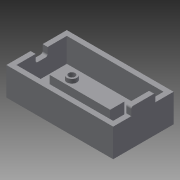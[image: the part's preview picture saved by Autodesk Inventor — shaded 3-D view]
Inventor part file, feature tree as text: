
AUTODESK INVENTOR PART (.ipt)
format: ipt  version: 2015 (Build 190159000, 159)  size: 167,424 bytes
history: native  units: mm
features: extrude x7, sketch x7, hole x1, fillet x1
ambient origin geometry x8: Origin, YZ Plane, XZ Plane, XY Plane, X Axis, Y Axis, Z Axis, Center Point
bodies: Volumenkörper1 (feature_tree)
feature tree (16):
  extrude  "Extrusion1"  Depth=53.0mm
  extrude  "Extrusion2"  Depth=25.0mm
  extrude  "Extrusion3"  Depth=2.5mm
  hole  "Bohrung1"  [1 undecoded]
  extrude  "Extrusion4"  Depth=12.0mm TaperAngle=0.0deg
  extrude  "Extrusion5"  Depth=30.0mm
  extrude  "Extrusion6"  Depth=9.0mm
  extrude  "Extrusion7"  Depth=9.0mm
  fillet  "Rundung1"  Radius=7.0mm
  sketch  "Skizze1"  dims[d0=30.0mm d1=53.0mm]
  sketch  "Skizze2"  dims[d2=2.0mm d3=0.0mm d4=25.0mm]
  sketch  "Skizze3"  dims[d5=48.0mm d6=2.5mm]
  sketch  "Skizze4"  dims[d7=2.5mm d8=2.5mm]
  sketch  "Skizze5"  dims[d9=2.5mm d10=12.0mm d11=0.0mm]
  sketch  "Skizze6"  dims[d12=10.0mm d13=30.0mm]
  sketch  "Skizze7"  dims[d14=7.0mm d15=9.0mm d16=9.0mm d17=7.0mm d18=0.0mm d19=15.0mm d20=12.5mm d21=3.2mm d22=6.0mm d23=4.0mm d24=2.0mm d25=90.0deg d26=8.0mm d27=20.594885mm d28=6.2mm d29=12.5mm d30=15.0mm d31=5.0mm d32=0.0mm d33=5.0mm d34=15.0mm d35=3.5mm d36=2.0mm d37=0.0mm d38=12.0mm d39=9.0mm d40=9.0mm d41=4.0mm d42=0.0mm d43=6.0mm d44=12.0mm d45=12.0mm d46=4.0mm d47=0.0mm d48=1.0mm]
note: 1 required parameter value undecoded (feature->parameter linkage not recoverable at this tier; creation-order binding heuristic only, values carry confidence <= 0.55)
